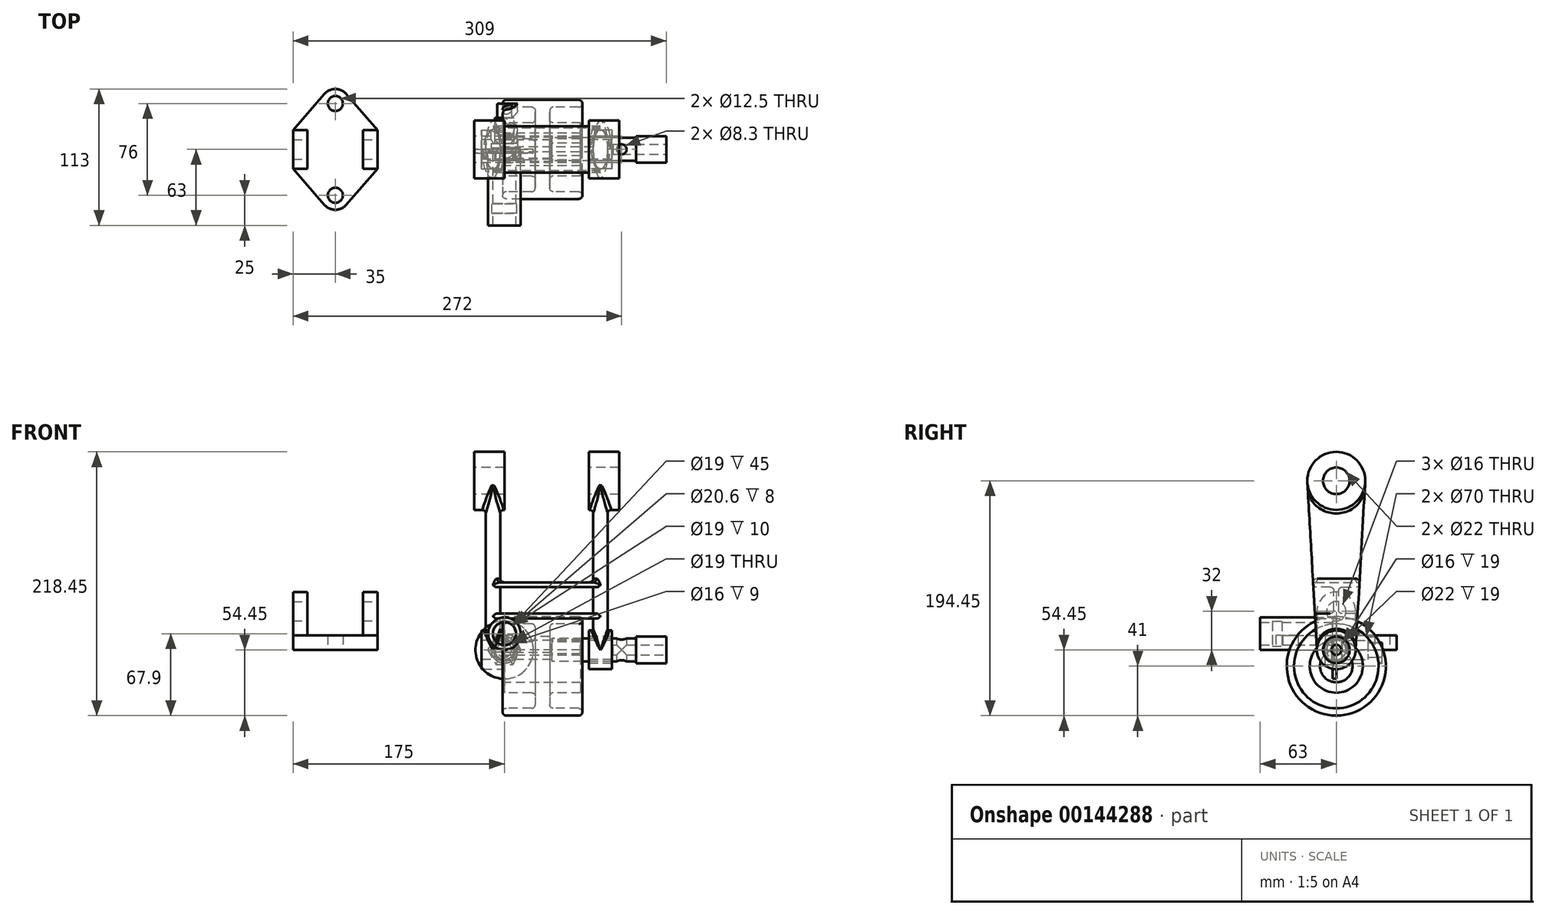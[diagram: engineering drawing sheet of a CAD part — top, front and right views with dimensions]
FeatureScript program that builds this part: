
annotation { "Feature Type Name" : "Feature", "Feature Type Description" : "" }
export const myFeature = defineFeature(function(context is Context, id is Id, definition is map)
    precondition{}
    {
        {
            assignVariable(context, id + "F0", {"name" : "gap", "anyValue" : 70});
        }
        {
            var Q0;
            Q0=qCreatedBy(makeId("Right.planeOp"),FACE);
            var sketch = newSketch(context, id + "F1", { "sketchPlane" : qUnion([Q0])});
            skCircle(sketch, "E0", {"center": v(0, 0) * mm, "radius": 16 * mm});
            skCircle(sketch, "E1", {"center": v(0, 140) * mm, "radius": 24 * mm});
            skSolve(sketch);
        }
        {
            var Q0;
            Q0=makeQuery(id+"F1.imprint","IMPRINT",FACE,{"disambiguationData":[TD([[makeQuery(id+"F1.imprint","IMPRINT",EDGE,{"derivedFrom":sQuery(id+"F1.wireOp",EDGE,"E1")}),1.0]])]});
            extrude(context, id + "F2", {"entities" : qUnion([Q0]), "oppositeDirection" : true, "depth" : 25 * mm});
        }
        {
            var Q0;
            Q0=makeQuery(id+"F1.imprint","IMPRINT",FACE,{"disambiguationData":[TD([[makeQuery(id+"F1.imprint","IMPRINT",EDGE,{"derivedFrom":sQuery(id+"F1.wireOp",EDGE,"E0")}),1.0]])]});
            extrude(context, id + "F3", {"entities" : qUnion([Q0]), "oppositeDirection" : true, "depth" : 19 * mm});
        }
        {
            var Q0;
            Q0=qCreatedBy(makeId("Top.planeOp"),FACE);
            var sketch = newSketch(context, id + "F4", { "sketchPlane" : qUnion([Q0])});
            skEllipse(sketch, "E2", {"center": v(-9.5, 0) * mm, "majorRadius": 16 * mm, "minorRadius": 6 * mm, "majorAxis": v(0, 1)});
            skLineSegment(sketch, "E3", {"start": v(-19, 16) * mm, "end": v(0, 16) * mm, "construction": true});
            skPoint(sketch, "E4", {"position": v(-15.5, 0) * mm});
            skSolve(sketch);
        }
        {
            var Q0;
            Q0=sQuery(id+"F1.wireOp",VERTEX,"E1.center");
            var Q1;
            Q1=qCreatedBy(makeId("Top.planeOp"),FACE);
            cPlane(context, id + "F5", {"entities" : qUnion([Q0, Q1]), "cplaneType" : CPlaneType.PLANE_POINT, "offset" : 25 * mm, "width" : 150 * mm, "height" : 150 * mm});
        }
        {
            var Q0;
            Q0=qCreatedBy(id+"F5.planeOp",FACE);
            var sketch = newSketch(context, id + "F6", { "sketchPlane" : qUnion([Q0])});
            skLineSegment(sketch, "E5", {"start": v(-25, 24) * mm, "end": v(0, 24) * mm, "construction": true});
            skEllipse(sketch, "E6", {"center": v(-9.5, 0) * mm, "majorRadius": 24 * mm, "minorRadius": 6 * mm, "majorAxis": v(0, 1)});
            skSolve(sketch);
        }
        {
            var Q2;
            Q2 = qSketchRegion(id + "F6", true);
            var Q3;
            Q3 = qSketchRegion(id + "F4", true);
            loft(context, id + "F7", {"operationType" : NewBodyOperationType.ADD, "sheetProfilesArray" : [{ "sheetProfileEntities" : qUnion([Q2]) }, { "sheetProfileEntities" : qUnion([Q3]) }]});
        }
        {
            var Q0;
            Q0=makeQuery(id+"F2.opExtrude","SWEPT_BODY",BODY,{"disambiguationData":[OSD([sQuery(id+"F1.wireOp",EDGE,"E1")])]});
            transform(context, id + "F8", {"entities" : qUnion([Q0]), "transformType" : TransformType.TRANSLATION_3D, "dx" : (getVariable(context, 'gap')) * mm, "dy" : 0 * mm, "dz" : 0 * mm, "makeCopy" : true});
        }
        {
            var Q0;
            Q0=makeQuery(id+"F8.opPattern","COPY",FACE,{"derivedFrom":makeQuery(id+"F2.opExtrude","CAP_FACE",FACE,{"disambiguationData":[OSD([sQuery(id+"F1.wireOp",EDGE,"E1")])],"isStart":true}),"instanceName":"1"});
            var sketch = newSketch(context, id + "F9", { "sketchPlane" : qUnion([Q0])});
            skLineSegment(sketch, "E7", {"start": v(0, 140) * mm, "end": v(0, -24.66) * mm, "construction": true});
            skSolve(sketch);
        }
        {
            var Q0;
            Q0=makeQuery(id+"F8.opPattern","COPY",BODY,{"derivedFrom":makeQuery(id+"F2.opExtrude","SWEPT_BODY",BODY,{"disambiguationData":[OSD([sQuery(id+"F1.wireOp",EDGE,"E1")])]}),"instanceName":"1"});
            var Q1;
            Q1=sQuery(id+"F9.wireOp",EDGE,"E7");
            transform(context, id + "F10", {"entities" : qUnion([Q0]), "transformType" : TransformType.ROTATION, "transformAxis" : qUnion([Q1]), "angle" : 180 * degree, "makeCopy" : false});
        }
        {
            var Q0;
            Q0=qCreatedBy(makeId("Right.planeOp"),FACE);
            cPlane(context, id + "F11", {"entities" : qUnion([Q0]), "cplaneType" : CPlaneType.OFFSET, "offset" : 9.5 * mm, "oppositeDirection" : true, "width" : 150 * mm, "height" : 150 * mm});
        }
        {
            var Q0;
            Q0=qCreatedBy(id+"F11.planeOp",FACE);
            var sketch = newSketch(context, id + "F12", { "sketchPlane" : qUnion([Q0])});
            skCircle(sketch, "E8.0", {"center": v(0, 140) * mm, "radius": 24 * mm, "construction": true});
            skCircle(sketch, "E9.0", {"center": v(0, 0) * mm, "radius": 16 * mm, "construction": true});
            skLineSegment(sketch, "E10", {"start": v(-23.96, 138.63) * mm, "end": v(-15.97, -0.91) * mm, "construction": true});
            skLineSegment(sketch, "E11", {"start": v(23.96, 138.63) * mm, "end": v(15.97, -0.91) * mm, "construction": true});
            skLineSegment(sketch, "E12", {"start": v(15.63, 26) * mm, "end": v(-15.63, 26) * mm});
            skArc(sketch, "E13", {"start": v(-15.63, 30) * mm, "mid": v(-17.63, 28) * mm, "end": v(-15.63, 26) * mm});
            skArc(sketch, "E14", {"start": v(15.63, 26) * mm, "mid": v(17.63, 28) * mm, "end": v(15.63, 30) * mm});
            skLineSegment(sketch, "E15", {"start": v(-17.11, 56) * mm, "end": v(17.11, 56) * mm});
            skArc(sketch, "E16", {"start": v(-17.11, 56) * mm, "mid": v(-19.11, 54) * mm, "end": v(-17.11, 52) * mm});
            skArc(sketch, "E17", {"start": v(17.11, 52) * mm, "mid": v(19.11, 54) * mm, "end": v(17.11, 56) * mm});
            skLineSegment(sketch, "E18", {"start": v(-17.11, 52) * mm, "end": v(-5, 52) * mm});
            skLineSegment(sketch, "E19", {"start": v(-2, 49) * mm, "end": v(-2, 33) * mm});
            skLineSegment(sketch, "E20", {"start": v(-5, 30) * mm, "end": v(-15.63, 30) * mm});
            skLineSegment(sketch, "E21", {"start": v(17.11, 52) * mm, "end": v(5, 52) * mm});
            skLineSegment(sketch, "E22", {"start": v(2, 49) * mm, "end": v(2, 33) * mm});
            skLineSegment(sketch, "E23", {"start": v(5, 30) * mm, "end": v(15.63, 30) * mm});
            skPoint(sketch, "E24.visualSharp", {"position": v(-2, 52) * mm});
            skArc(sketch, "E24.filletArc", {"start": v(-2, 49) * mm, "mid": v(-2.88, 51.12) * mm, "end": v(-5, 52) * mm});
            skPoint(sketch, "E25.visualSharp", {"position": v(2, 52) * mm});
            skArc(sketch, "E25.filletArc", {"start": v(5, 52) * mm, "mid": v(2.88, 51.12) * mm, "end": v(2, 49) * mm});
            skPoint(sketch, "E26.visualSharp", {"position": v(2, 30) * mm});
            skArc(sketch, "E26.filletArc", {"start": v(2, 33) * mm, "mid": v(2.88, 30.88) * mm, "end": v(5, 30) * mm});
            skPoint(sketch, "E27.visualSharp", {"position": v(-2, 30) * mm});
            skArc(sketch, "E27.filletArc", {"start": v(-5, 30) * mm, "mid": v(-2.88, 30.88) * mm, "end": v(-2, 33) * mm});
            skSolve(sketch);
        }
        {
            var Q0;
            Q0 = qSketchRegion(id + "F12", true);
            var Q1;
            Q1=makeQuery(id+"F8.opPattern","COPY",BODY,{"derivedFrom":makeQuery(id+"F2.opExtrude","SWEPT_BODY",BODY,{"disambiguationData":[OSD([sQuery(id+"F1.wireOp",EDGE,"E1")])]}),"instanceName":"1"});
            extrude(context, id + "F13", {"entities" : qUnion([Q0]), "operationType" : NewBodyOperationType.ADD, "endBoundEntityBody" : qUnion([Q1]), "depth" : (getVariable(context, 'gap') + 19) * mm});
        }
        {
            var Q0;
            Q0=qCreatedBy(makeId("Top.planeOp"),FACE);
            var sketch = newSketch(context, id + "F14", { "sketchPlane" : qUnion([Q0])});
            skLineSegment(sketch, "E28", {"start": v(-175, 16) * mm, "end": v(-149.06, 45.87) * mm});
            skLineSegment(sketch, "E29", {"start": v(-130.94, 45.87) * mm, "end": v(-105, 16) * mm});
            skLineSegment(sketch, "E30", {"start": v(-105, -16) * mm, "end": v(-130.94, -45.87) * mm});
            skLineSegment(sketch, "E31", {"start": v(-149.06, -45.87) * mm, "end": v(-175, -16) * mm});
            skLineSegment(sketch, "E32", {"start": v(-175, 16) * mm, "end": v(-175, -16) * mm});
            skLineSegment(sketch, "E33", {"start": v(-105, 16) * mm, "end": v(-105, -16) * mm});
            skArc(sketch, "E34", {"start": v(-130.94, 45.87) * mm, "mid": v(-140, 50) * mm, "end": v(-149.06, 45.87) * mm});
            skArc(sketch, "E35", {"start": v(-149.06, -45.87) * mm, "mid": v(-140, -50) * mm, "end": v(-130.94, -45.87) * mm});
            skCircle(sketch, "E36", {"center": v(-140, 38) * mm, "radius": 6.25 * mm});
            skCircle(sketch, "E37", {"center": v(-140, -38) * mm, "radius": 6.25 * mm});
            skSolve(sketch);
        }
        {
            var Q0;
            Q0=makeQuery(id+"F2.opExtrude","CAP_FACE",FACE,{"disambiguationData":[OSD([sQuery(id+"F1.wireOp",EDGE,"E1")])],"isStart":false});
            var sketch = newSketch(context, id + "F15", { "sketchPlane" : qUnion([Q0])});
            skCircle(sketch, "E38", {"center": v(0, 140) * mm, "radius": 11 * mm});
            skCircle(sketch, "E39", {"center": v(0, 0) * mm, "radius": 8 * mm});
            skSolve(sketch);
        }
        {
            var Q0;
            Q0 = qSketchRegion(id + "F15", true);
            extrude(context, id + "F16", {"entities" : qUnion([Q0]), "operationType" : NewBodyOperationType.REMOVE, "endBound" : BoundingType.THROUGH_ALL, "oppositeDirection" : true, "depth" : 25 * mm});
        }
        {
            var Q0;
            Q0=makeQuery(id+"F13.boolean.opBoolean","INTERSECT",EDGE,{"derivedFrom":[makeQuery(id+"F7.opLoft","SWEPT_FACE",FACE,{"disambiguationData":[OSD([sQuery(id+"F4.wireOp",EDGE,"E2"),sQuery(id+"F6.wireOp",EDGE,"E6")])]}),makeQuery(id+"F13.opExtrude","SWEPT_FACE",FACE,{"disambiguationData":[OSD([sQuery(id+"F12.wireOp",EDGE,"E15")])]})]});
            var Q1;
            Q1=makeQuery(id+"F13.boolean.opBoolean","INTERSECT",EDGE,{"derivedFrom":[makeQuery(id+"F8.opPattern","COPY",FACE,{"derivedFrom":makeQuery(id+"F7.opLoft","SWEPT_FACE",FACE,{"disambiguationData":[OSD([sQuery(id+"F4.wireOp",EDGE,"E2"),sQuery(id+"F6.wireOp",EDGE,"E6")])]}),"instanceName":"1"}),makeQuery(id+"F13.opExtrude","SWEPT_FACE",FACE,{"disambiguationData":[OSD([sQuery(id+"F12.wireOp",EDGE,"E15")])]})]});
            var Q2;
            Q2=makeQuery(id+"F7.boolean.opBoolean","INTERSECT",EDGE,{"derivedFrom":[makeQuery(id+"F2.opExtrude","SWEPT_FACE",FACE,{"disambiguationData":[OSD([sQuery(id+"F1.wireOp",EDGE,"E1")])]}),makeQuery(id+"F7.opLoft","SWEPT_FACE",FACE,{"disambiguationData":[OSD([sQuery(id+"F4.wireOp",EDGE,"E2"),sQuery(id+"F6.wireOp",EDGE,"E6")])]})]});
            var Q3;
            Q3=makeQuery(id+"F8.opPattern","COPY",EDGE,{"derivedFrom":makeQuery(id+"F7.boolean.opBoolean","INTERSECT",EDGE,{"derivedFrom":[makeQuery(id+"F2.opExtrude","SWEPT_FACE",FACE,{"disambiguationData":[OSD([sQuery(id+"F1.wireOp",EDGE,"E1")])]}),makeQuery(id+"F7.opLoft","SWEPT_FACE",FACE,{"disambiguationData":[OSD([sQuery(id+"F4.wireOp",EDGE,"E2"),sQuery(id+"F6.wireOp",EDGE,"E6")])]})]}),"instanceName":"1"});
            fillet(context, id + "F17", {"entities" : qUnion([Q0, Q1, Q2, Q3]), "radius" : 3 * mm, "tangentPropagation" : true, "allowEdgeOverflow" : false});
        }
        {
            var Q0;
            Q0=makeQuery(id+"F8.opPattern","COPY",EDGE,{"derivedFrom":makeQuery(id+"F7.boolean.opBoolean","INTERSECT",EDGE,{"derivedFrom":[makeQuery(id+"F3.opExtrude","SWEPT_FACE",FACE,{"disambiguationData":[OSD([sQuery(id+"F1.wireOp",EDGE,"E0")])]}),makeQuery(id+"F7.opLoft","SWEPT_FACE",FACE,{"disambiguationData":[OSD([sQuery(id+"F4.wireOp",EDGE,"E2"),sQuery(id+"F6.wireOp",EDGE,"E6")])]})]}),"instanceName":"1"});
            var Q1;
            Q1=makeQuery(id+"F7.boolean.opBoolean","INTERSECT",EDGE,{"derivedFrom":[makeQuery(id+"F3.opExtrude","SWEPT_FACE",FACE,{"disambiguationData":[OSD([sQuery(id+"F1.wireOp",EDGE,"E0")])]}),makeQuery(id+"F7.opLoft","SWEPT_FACE",FACE,{"disambiguationData":[OSD([sQuery(id+"F4.wireOp",EDGE,"E2"),sQuery(id+"F6.wireOp",EDGE,"E6")])]})]});
            fillet(context, id + "F18", {"entities" : qUnion([Q0, Q1]), "radius" : 1.5 * mm, "tangentPropagation" : true, "allowEdgeOverflow" : false});
        }
        {
            var Q0;
            Q0=qCreatedBy(makeId("Front.planeOp"),FACE);
            var sketch = newSketch(context, id + "F19", { "sketchPlane" : qUnion([Q0])});
            skLineSegment(sketch, "E40", {"start": v(0, 0) * mm, "end": v(63, 0) * mm});
            skLineSegment(sketch, "E41", {"start": v(63, 0) * mm, "end": v(63, 8.55) * mm});
            skLineSegment(sketch, "E42", {"start": v(63, 8.55) * mm, "end": v(40.5, 8.55) * mm});
            skLineSegment(sketch, "E43", {"start": v(37.5, 11.55) * mm, "end": v(37.5, 18.55) * mm});
            skLineSegment(sketch, "E44", {"start": v(40.5, 21.55) * mm, "end": v(61.5, 21.55) * mm});
            skArc(sketch, "E45", {"start": v(61.5, 21.55) * mm, "mid": v(64.5, 24.55) * mm, "end": v(61.5, 27.55) * mm});
            skLineSegment(sketch, "E46", {"start": v(61.5, 27.55) * mm, "end": v(1.5, 27.55) * mm});
            skArc(sketch, "E47", {"start": v(1.5, 27.55) * mm, "mid": v(-1.5, 24.55) * mm, "end": v(1.5, 21.55) * mm});
            skLineSegment(sketch, "E48", {"start": v(1.5, 21.55) * mm, "end": v(22.5, 21.55) * mm});
            skLineSegment(sketch, "E49", {"start": v(25.5, 18.55) * mm, "end": v(25.5, 11.55) * mm});
            skLineSegment(sketch, "E50", {"start": v(22.5, 8.55) * mm, "end": v(0, 8.55) * mm});
            skLineSegment(sketch, "E51", {"start": v(0, 8.55) * mm, "end": v(0, 0) * mm});
            skPoint(sketch, "E52.visualSharp", {"position": v(37.5, 8.55) * mm});
            skArc(sketch, "E52.filletArc", {"start": v(37.5, 11.55) * mm, "mid": v(38.38, 9.43) * mm, "end": v(40.5, 8.55) * mm});
            skPoint(sketch, "E53.visualSharp", {"position": v(25.5, 8.55) * mm});
            skArc(sketch, "E53.filletArc", {"start": v(22.5, 8.55) * mm, "mid": v(24.62, 9.43) * mm, "end": v(25.5, 11.55) * mm});
            skLineSegment(sketch, "E54", {"start": v(0, -13.45) * mm, "end": v(71.85, -13.45) * mm, "construction": true});
            skPoint(sketch, "E55.visualSharp", {"position": v(25.5, 21.55) * mm});
            skArc(sketch, "E55.filletArc", {"start": v(25.5, 18.55) * mm, "mid": v(24.62, 20.67) * mm, "end": v(22.5, 21.55) * mm});
            skPoint(sketch, "E56.visualSharp", {"position": v(37.5, 21.55) * mm});
            skArc(sketch, "E56.filletArc", {"start": v(40.5, 21.55) * mm, "mid": v(38.38, 20.67) * mm, "end": v(37.5, 18.55) * mm});
            skSolve(sketch);
        }
        {
            var Q0;
            Q0=makeQuery(id+"F19.imprint","IMPRINT",FACE,{"disambiguationData":[TD([[makeQuery(id+"F19.imprint","IMPRINT",EDGE,{"derivedFrom":sQuery(id+"F19.wireOp",EDGE,"E40")}),1.0]])]});
            var Q1;
            Q1=sQuery(id+"F19.wireOp",EDGE,"E54");
            revolve(context, id + "F20", {"entities" : qUnion([Q0]), "axis" : qUnion([Q1]), "revolveType" : RevolveType.FULL});
        }
        {
            var Q0;
            Q0=qCreatedBy(makeId("Right.planeOp"),FACE);
            var sketch = newSketch(context, id + "F21", { "sketchPlane" : qUnion([Q0])});
            skLineSegment(sketch, "E57", {"start": v(0, 0) * mm, "end": v(-63, 0) * mm});
            skLineSegment(sketch, "E58", {"start": v(-63, 0) * mm, "end": v(-63, 3.95) * mm});
            skLineSegment(sketch, "E59", {"start": v(-63, 3.95) * mm, "end": v(-53, 3.95) * mm});
            skLineSegment(sketch, "E60", {"start": v(-53, 3.95) * mm, "end": v(-53, 3.15) * mm});
            skLineSegment(sketch, "E61", {"start": v(-53, 3.15) * mm, "end": v(-45, 3.15) * mm});
            skLineSegment(sketch, "E62", {"start": v(-45, 3.15) * mm, "end": v(-45, 3.95) * mm});
            skLineSegment(sketch, "E63", {"start": v(-45, 3.95) * mm, "end": v(0, 3.95) * mm});
            skLineSegment(sketch, "E64", {"start": v(0, 3.95) * mm, "end": v(0, 0) * mm});
            skLineSegment(sketch, "E65", {"start": v(0, 13.45) * mm, "end": v(-63, 13.45) * mm, "construction": true});
            skPoint(sketch, "E65.startSnap0", {"position": v(0, 1.98) * mm});
            skSolve(sketch);
        }
        {
            var Q0;
            Q0=makeQuery(id+"F21.imprint","IMPRINT",FACE,{"disambiguationData":[TD([[makeQuery(id+"F21.imprint","IMPRINT",EDGE,{"derivedFrom":sQuery(id+"F21.wireOp",EDGE,"E57")}),-1.0]])]});
            var Q1;
            Q1=sQuery(id+"F21.wireOp",EDGE,"E65");
            revolve(context, id + "F22", {"entities" : qUnion([Q0]), "axis" : qUnion([Q1]), "revolveType" : RevolveType.FULL});
        }
        {
            var Q0;
            Q0 = qSketchRegion(id + "F14", true);
            extrude(context, id + "F23", {"entities" : qUnion([Q0]), "depth" : 12 * mm});
        }
        {
            var Q0;
            Q0=qCreatedBy(makeId("Right.planeOp"),FACE);
            var sketch = newSketch(context, id + "F24", { "sketchPlane" : qUnion([Q0])});
            skCircle(sketch, "E66", {"center": v(0, 0) * mm, "radius": 11 * mm});
            skSolve(sketch);
        }
        {
            var Q0;
            Q0 = qSketchRegion(id + "F24", true);
            extrude(context, id + "F25", {"entities" : qUnion([Q0]), "depth" : 134 * mm});
        }
        {
            var Q0;
            Q0=makeQuery(id+"F25.opExtrude","CAP_FACE",FACE,{"disambiguationData":[OSD([sQuery(id+"F24.wireOp",EDGE,"E66")])],"isStart":false});
            var sketch = newSketch(context, id + "F26", { "sketchPlane" : qUnion([Q0])});
            skCircle(sketch, "E67", {"center": v(0, 0) * mm, "radius": 4.15 * mm});
            skSolve(sketch);
        }
        {
            var Q0;
            Q0 = qSketchRegion(id + "F26", true);
            extrude(context, id + "F27", {"entities" : qUnion([Q0]), "operationType" : NewBodyOperationType.REMOVE, "oppositeDirection" : true, "depth" : 44 * mm});
        }
        {
            var Q0;
            Q0=qCreatedBy(makeId("Top.planeOp"),FACE);
            var sketch = newSketch(context, id + "F28", { "sketchPlane" : qUnion([Q0])});
            skCircle(sketch, "E68", {"center": v(97, 0) * mm, "radius": 4.15 * mm});
            skSolve(sketch);
        }
        {
            var Q0;
            Q0 = qSketchRegion(id + "F28", true);
            extrude(context, id + "F29", {"entities" : qUnion([Q0]), "operationType" : NewBodyOperationType.REMOVE, "endBound" : BoundingType.SYMMETRIC, "depth" : 25 * mm});
        }
        {
            var Q0;
            Q0=makeQuery(id+"F25.opExtrude","CAP_FACE",FACE,{"disambiguationData":[OSD([sQuery(id+"F24.wireOp",EDGE,"E66")])],"isStart":true});
            var sketch = newSketch(context, id + "F30", { "sketchPlane" : qUnion([Q0])});
            skCircle(sketch, "E69", {"center": v(0, 0) * mm, "radius": 9.5 * mm});
            skSolve(sketch);
        }
        {
            var Q0;
            Q0=makeQuery(id+"F30.imprint","IMPRINT",FACE,{"disambiguationData":[TD([[makeQuery(id+"F30.imprint","IMPRINT",EDGE,{"derivedFrom":sQuery(id+"F30.wireOp",EDGE,"E69")}),-1.0]])]});
            extrude(context, id + "F31", {"entities" : qUnion([Q0]), "operationType" : NewBodyOperationType.REMOVE, "oppositeDirection" : true, "depth" : 109 * mm});
        }
        {
            var Q0;
            Q0=makeQuery(id+"F25.opExtrude","CAP_FACE",FACE,{"disambiguationData":[OSD([sQuery(id+"F24.wireOp",EDGE,"E66")])],"isStart":true});
            var sketch = newSketch(context, id + "F32", { "sketchPlane" : qUnion([Q0])});
            skCircle(sketch, "E70", {"center": v(0, 0) * mm, "radius": 8 * mm});
            skSolve(sketch);
        }
        {
            var Q0;
            Q0=makeQuery(id+"F32.imprint","IMPRINT",FACE,{"disambiguationData":[TD([[makeQuery(id+"F32.imprint","IMPRINT",EDGE,{"derivedFrom":sQuery(id+"F32.wireOp",EDGE,"E70")}),-1.0]])]});
            extrude(context, id + "F33", {"entities" : qUnion([Q0]), "operationType" : NewBodyOperationType.REMOVE, "oppositeDirection" : true, "depth" : 39 * mm});
        }
        {
            var Q0;
            Q0=qCreatedBy(makeId("Front.planeOp"),FACE);
            var sketch = newSketch(context, id + "F34", { "sketchPlane" : qUnion([Q0])});
            skCircle(sketch, "E71", {"center": v(0, 0) * mm, "radius": 24 * mm});
            skCircle(sketch, "E72", {"center": v(0, 0) * mm, "radius": 9.5 * mm});
            skSolve(sketch);
        }
        {
            var Q0;
            Q0=makeQuery(id+"F34.imprint","IMPRINT",FACE,{"disambiguationData":[TD([[makeQuery(id+"F34.imprint","IMPRINT",EDGE,{"derivedFrom":sQuery(id+"F34.wireOp",EDGE,"E71")}),1.0]])]});
            extrude(context, id + "F35", {"entities" : qUnion([Q0]), "depth" : 3 * mm});
        }
        {
            var Q0;
            Q0=qCreatedBy(makeId("Front.planeOp"),FACE);
            var sketch = newSketch(context, id + "F36", { "sketchPlane" : qUnion([Q0])});
            skCircle(sketch, "E73.cCircle", {"center": v(0, 0) * mm, "radius": 12 * mm, "construction": true});
            skLineSegment(sketch, "E73.0", {"start": v(6.93, 12) * mm, "end": v(13.86, 0) * mm});
            skLineSegment(sketch, "E73.1", {"start": v(13.86, 0) * mm, "end": v(6.93, -12) * mm});
            skLineSegment(sketch, "E73.2", {"start": v(6.93, -12) * mm, "end": v(-6.93, -12) * mm});
            skLineSegment(sketch, "E73.3", {"start": v(-6.93, -12) * mm, "end": v(-13.86, 0) * mm});
            skLineSegment(sketch, "E73.4", {"start": v(-13.86, 0) * mm, "end": v(-6.93, 12) * mm});
            skLineSegment(sketch, "E73.5", {"start": v(-6.93, 12) * mm, "end": v(6.93, 12) * mm});
            skPoint(sketch, "E73.0.midPoint", {"position": v(10.4, 6) * mm});
            skCircle(sketch, "E74", {"center": v(0, 0) * mm, "radius": 8 * mm});
            skSolve(sketch);
        }
        {
            var Q0;
            Q0=makeQuery(id+"F36.imprint","IMPRINT",FACE,{"disambiguationData":[TD([[makeQuery(id+"F36.imprint","IMPRINT",EDGE,{"derivedFrom":sQuery(id+"F36.wireOp",EDGE,"E73.0")}),-1.0]])]});
            extrude(context, id + "F37", {"entities" : qUnion([Q0]), "depth" : 9 * mm});
        }
        {
            var Q0;
            Q0=makeQuery(id+"F37.opExtrude","CAP_EDGE",EDGE,{"disambiguationData":[OSD([sQuery(id+"F36.wireOp",EDGE,"E73.5")])],"isStart":true});
            var Q1;
            Q1=makeQuery(id+"F37.opExtrude","CAP_EDGE",EDGE,{"disambiguationData":[OSD([sQuery(id+"F36.wireOp",EDGE,"E73.0")])],"isStart":true});
            var Q2;
            Q2=makeQuery(id+"F37.opExtrude","CAP_EDGE",EDGE,{"disambiguationData":[OSD([sQuery(id+"F36.wireOp",EDGE,"E73.1")])],"isStart":true});
            var Q3;
            Q3=makeQuery(id+"F37.opExtrude","CAP_EDGE",EDGE,{"disambiguationData":[OSD([sQuery(id+"F36.wireOp",EDGE,"E73.2")])],"isStart":true});
            var Q4;
            Q4=makeQuery(id+"F37.opExtrude","CAP_EDGE",EDGE,{"disambiguationData":[OSD([sQuery(id+"F36.wireOp",EDGE,"E73.3")])],"isStart":true});
            var Q5;
            Q5=makeQuery(id+"F37.opExtrude","CAP_EDGE",EDGE,{"disambiguationData":[OSD([sQuery(id+"F36.wireOp",EDGE,"E73.4")])],"isStart":true});
            chamfer(context, id + "F38", {"entities" : qUnion([Q0, Q1, Q2, Q3, Q4, Q5]), "chamferType" : ChamferType.OFFSET_ANGLE, "width" : 3 * mm, "oppositeDirection" : false, "angle" : 30 * degree, "tangentPropagation" : true});
        }
        {
            var Q0;
            Q0=qCreatedBy(makeId("Front.planeOp"),FACE);
            var sketch = newSketch(context, id + "F39", { "sketchPlane" : qUnion([Q0])});
            skCircle(sketch, "E75", {"center": v(0, 0) * mm, "radius": 11 * mm});
            skSolve(sketch);
        }
        {
            var Q0;
            Q0 = qSketchRegion(id + "F39", true);
            extrude(context, id + "F40", {"entities" : qUnion([Q0]), "oppositeDirection" : true, "depth" : 38 * mm});
        }
        {
            var Q0;
            Q0=makeQuery(id+"F40.opExtrude","CAP_EDGE",EDGE,{"disambiguationData":[OSD([sQuery(id+"F39.wireOp",EDGE,"E75")])],"isStart":true});
            fillet(context, id + "F41", {"entities" : qUnion([Q0]), "radius" : 1.5 * mm, "tangentPropagation" : true, "allowEdgeOverflow" : false});
        }
        {
            var Q0;
            Q0=makeQuery(id+"F40.opExtrude","CAP_FACE",FACE,{"disambiguationData":[OSD([sQuery(id+"F39.wireOp",EDGE,"E75")])],"isStart":false});
            var sketch = newSketch(context, id + "F42", { "sketchPlane" : qUnion([Q0])});
            skCircle(sketch, "E76", {"center": v(0, 0) * mm, "radius": 8 * mm});
            skSolve(sketch);
        }
        {
            var Q0;
            Q0=makeQuery(id+"F42.imprint","IMPRINT",FACE,{"disambiguationData":[TD([[makeQuery(id+"F42.imprint","IMPRINT",EDGE,{"derivedFrom":sQuery(id+"F42.wireOp",EDGE,"E76")}),-1.0]])]});
            extrude(context, id + "F43", {"entities" : qUnion([Q0]), "operationType" : NewBodyOperationType.REMOVE, "oppositeDirection" : true, "depth" : 33 * mm});
        }
        {
            var Q0;
            Q0=makeQuery(id+"F40.opExtrude","CAP_FACE",FACE,{"disambiguationData":[OSD([sQuery(id+"F39.wireOp",EDGE,"E75")])],"isStart":false});
            var sketch = newSketch(context, id + "F44", { "sketchPlane" : qUnion([Q0])});
            skCircle(sketch, "E77", {"center": v(0, 0) * mm, "radius": 6 * mm});
            skSolve(sketch);
        }
        {
            var Q0;
            Q0=makeQuery(id+"F44.imprint","IMPRINT",FACE,{"disambiguationData":[TD([[makeQuery(id+"F44.imprint","IMPRINT",EDGE,{"derivedFrom":sQuery(id+"F44.wireOp",EDGE,"E77")}),-1.0]])]});
            extrude(context, id + "F45", {"entities" : qUnion([Q0]), "operationType" : NewBodyOperationType.REMOVE, "oppositeDirection" : true, "depth" : 12 * mm});
        }
        {
            var Q0;
            Q0=makeQuery(id+"F40.opExtrude","CAP_FACE",FACE,{"disambiguationData":[OSD([sQuery(id+"F39.wireOp",EDGE,"E75")])],"isStart":true});
            var sketch = newSketch(context, id + "F46", { "sketchPlane" : qUnion([Q0])});
            skLineSegment(sketch, "E78.bottom", {"start": v(-12.48, 1.5) * mm, "end": v(12.63, 1.5) * mm});
            skLineSegment(sketch, "E78.top", {"start": v(-12.48, -1.5) * mm, "end": v(12.63, -1.5) * mm});
            skLineSegment(sketch, "E78.left", {"start": v(-12.48, 1.5) * mm, "end": v(-12.48, -1.5) * mm});
            skLineSegment(sketch, "E78.right", {"start": v(12.63, 1.5) * mm, "end": v(12.63, -1.5) * mm});
            skSolve(sketch);
        }
        {
            var Q0;
            Q0 = qSketchRegion(id + "F46", true);
            extrude(context, id + "F47", {"entities" : qUnion([Q0]), "operationType" : NewBodyOperationType.REMOVE, "oppositeDirection" : true, "depth" : 1.5 * mm});
        }
        {
            var Q0;
            Q0=makeQuery(id+"F23.opExtrude","SWEPT_FACE",FACE,{"disambiguationData":[OSD([sQuery(id+"F14.wireOp",EDGE,"E33")])]});
            cPlane(context, id + "F48", {"entities" : qUnion([Q0]), "cplaneType" : CPlaneType.OFFSET, "offset" : 1 * mm, "width" : 150 * mm, "height" : 150 * mm});
        }
        {
            var Q0;
            Q0=qCreatedBy(id+"F48.planeOp",FACE);
            var sketch = newSketch(context, id + "F49", { "sketchPlane" : qUnion([Q0])});
            skLineSegment(sketch, "E79", {"start": v(-16, 0) * mm, "end": v(-16, 32) * mm});
            skLineSegment(sketch, "E80", {"start": v(16, 0) * mm, "end": v(16, 32) * mm});
            skArc(sketch, "E81", {"start": v(16, 32) * mm, "mid": v(0, 48) * mm, "end": v(-16, 32) * mm});
            skLineSegment(sketch, "E82", {"start": v(-16, 0) * mm, "end": v(16, 0) * mm});
            skCircle(sketch, "E83", {"center": v(0, 32) * mm, "radius": 8 * mm});
            skSolve(sketch);
        }
        {
            var Q0;
            Q0=makeQuery(id+"F49.imprint","IMPRINT",FACE,{"disambiguationData":[TD([[makeQuery(id+"F49.imprint","IMPRINT",EDGE,{"derivedFrom":sQuery(id+"F49.wireOp",EDGE,"E79")}),-1.0]])]});
            extrude(context, id + "F50", {"entities" : qUnion([Q0]), "operationType" : NewBodyOperationType.ADD, "oppositeDirection" : true, "depth" : 71 * mm});
        }
        {
            var Q0;
            Q0=makeQuery(id+"F50.opExtrude","SWEPT_FACE",FACE,{"disambiguationData":[OSD([sQuery(id+"F49.wireOp",EDGE,"E79")])]});
            var sketch = newSketch(context, id + "F51", { "sketchPlane" : qUnion([Q0])});
            skLineSegment(sketch, "E84.bottom", {"start": v(-163, 48) * mm, "end": v(-117, 48) * mm});
            skLineSegment(sketch, "E84.top", {"start": v(-163, 12) * mm, "end": v(-117, 12) * mm});
            skLineSegment(sketch, "E84.left", {"start": v(-163, 48) * mm, "end": v(-163, 12) * mm});
            skLineSegment(sketch, "E84.right", {"start": v(-117, 48) * mm, "end": v(-117, 12) * mm});
            skLineSegment(sketch, "E85.bottom", {"start": v(-105, 48) * mm, "end": v(-104, 48) * mm});
            skLineSegment(sketch, "E85.top", {"start": v(-105, 0) * mm, "end": v(-104, 0) * mm});
            skLineSegment(sketch, "E85.left", {"start": v(-105, 48) * mm, "end": v(-105, 0) * mm});
            skLineSegment(sketch, "E85.right", {"start": v(-104, 48) * mm, "end": v(-104, 0) * mm});
            skSolve(sketch);
        }
        {
            var Q0;
            Q0 = qSketchRegion(id + "F51", true);
            extrude(context, id + "F52", {"entities" : qUnion([Q0]), "operationType" : NewBodyOperationType.REMOVE, "endBound" : BoundingType.THROUGH_ALL, "oppositeDirection" : true, "depth" : 25 * mm});
        }
    });
